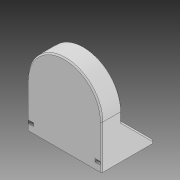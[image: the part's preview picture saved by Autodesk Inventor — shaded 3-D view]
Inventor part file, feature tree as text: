
AUTODESK INVENTOR PART (.ipt)
format: ipt  version: 2020 (Build 240168000, 168)  size: 419,328 bytes
history: native  units: mm
features: extrude x9, sketch x9, projected_geometry x2, mirror x1, plane x1, chamfer x1, fillet x1, revolve x1
ambient origin geometry x8: Origin, YZ Plane, XZ Plane, XY Plane, X Axis, Y Axis, Z Axis, Center Point
bodies: Solid1 (feature_tree)
feature tree (25):
  extrude  "Extrusion1"  Depth=70.0mm
  extrude  "Extrusion2"  Depth=2.0mm
  extrude  "Extrusion3"  Depth=1.0mm
  extrude  "Extrusion7"  Depth=50.0mm TaperAngle=360.0deg
  mirror  "Mirror1"
  extrude  "Extrusion4"  Depth=5.5mm
  plane  "Work Plane1"
  sketch  "Sketch6"  dims[d14=0.0mm d15=0.0mm d16=5.5mm]
  extrude  "Extrusion5"  Depth=6.5mm
  extrude  "Extrusion6"  Depth=18.0mm TaperAngle=0.0deg
  chamfer  "Chamfer1"  Distance=4.5mm
  fillet  "Fillet2"  Radius=20.75mm
  revolve  "Revolution1"  Angle=45.0deg
  extrude  "Extrusion8"  Depth=50.0mm
  extrude  "Extrusion9"  Depth=5.0mm
  sketch  "Sketch1"  dims[d0=95.05mm d2=70.0mm]
  sketch  "Sketch2"  dims[d3=32.5mm d4=0.0mm d5=2.0mm]
  sketch  "Sketch3"  dims[d6=1.0mm d7=0.0mm d8=5.2mm]
  sketch  "Sketch5"  dims[d9=55.0mm d10=50.0mm d12=360.0deg]
  sketch  "Sketch7"  dims[d17=6.5mm d18=6.5mm]
  projected_geometry  "Projected Loop2"
  sketch  "Sketch10"  dims[d19=6.5mm d20=18.0mm d21=0.0mm]
  projected_geometry  "Projected Loop4"
  sketch  "Sketch11"  dims[d22=-15.0mm]
  sketch  "Sketch12"  dims[d23=8.2mm d24=4.5mm d25=0.0mm d26=20.75mm d27=0.0mm d29=2.0mm d30=2.0mm d31=45.0deg d32=50.0mm d33=5.0mm d34=135.0deg d35=15.0mm d36=0.0mm d37=10.0mm d38=5.0mm d43=60.0mm d44=11.1mm d45=1.0mm d46=0.5mm d47=2.0mm d48=2.5mm d49=7.0mm d51=2.0mm d52=120.0deg d53=2.0mm d54=11.1mm d55=2.5mm d56=120.0deg d57=90.0deg d58=55.0mm d59=75.0mm d60=10.0mm d61=0.0mm d62=10.0mm d63=0.0mm]
